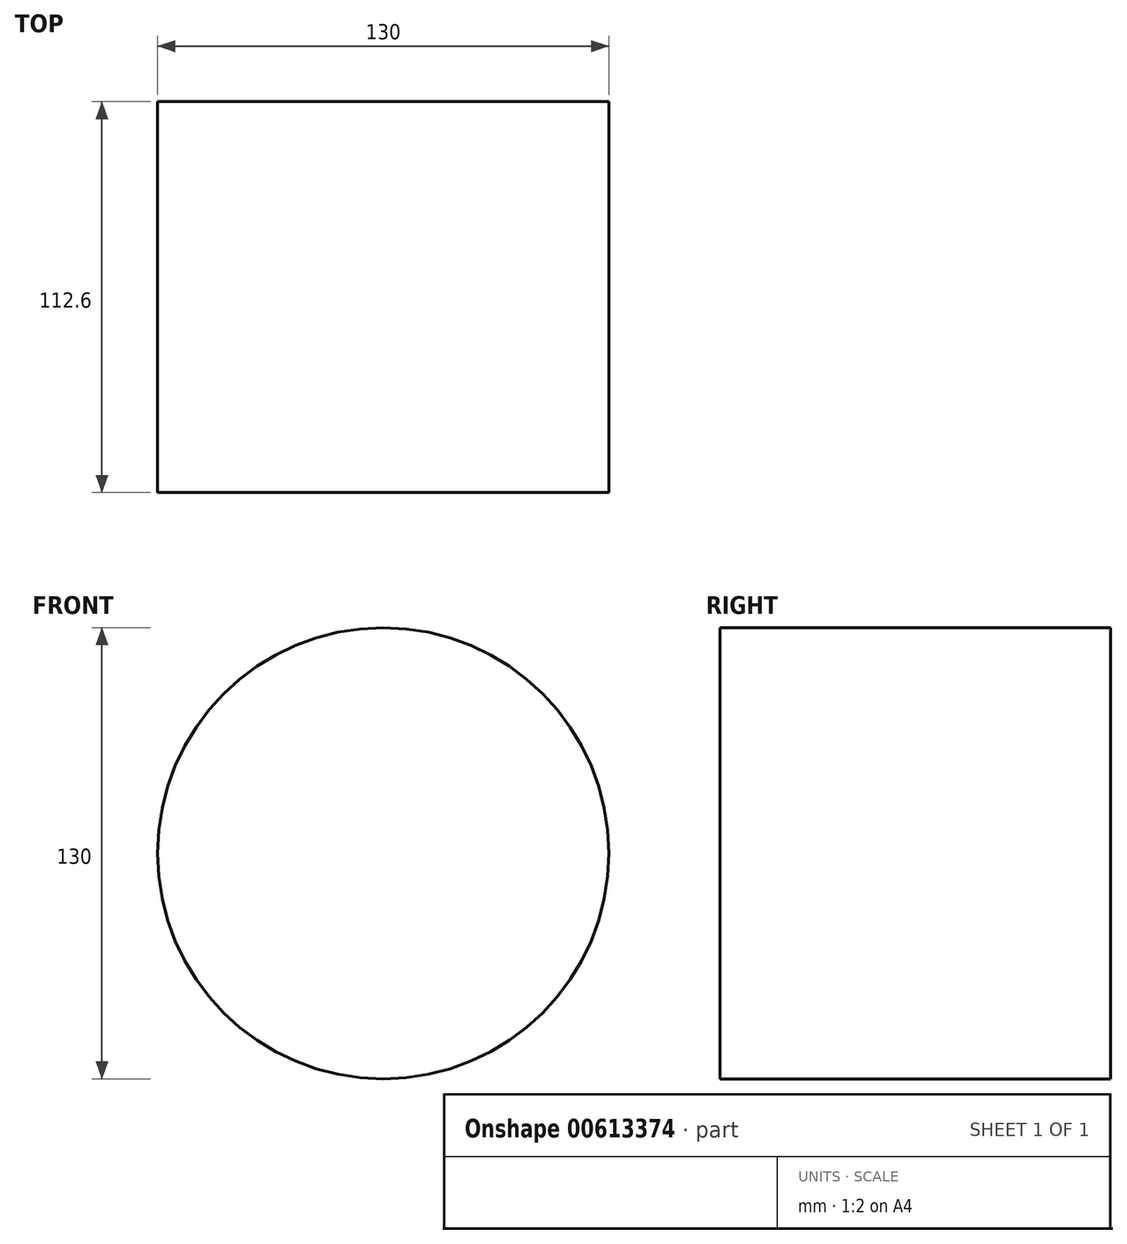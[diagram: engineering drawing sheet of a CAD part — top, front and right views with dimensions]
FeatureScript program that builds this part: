
annotation { "Feature Type Name" : "Feature", "Feature Type Description" : "" }
export const myFeature = defineFeature(function(context is Context, id is Id, definition is map)
    precondition{}
    {
        {
            var Q0;
            Q0=qCreatedBy(makeId("Front.planeOp"),FACE);
            var sketch = newSketch(context, id + "F0", { "sketchPlane" : qUnion([Q0])});
            skCircle(sketch, "E0", {"center": v(0, 0) * mm, "radius": 65 * mm});
            skSolve(sketch);
        }
        {
            var Q0;
            Q0=makeQuery(id+"F0.imprint","IMPRINT",FACE,{"disambiguationData":[TD([[makeQuery(id+"F0.imprint","IMPRINT",EDGE,{"derivedFrom":sQuery(id+"F0.wireOp",EDGE,"E0")}),1.0]])]});
            extrude(context, id + "F1", {"entities" : qUnion([Q0]), "depth" : 112.6 * mm, "offsetDistance" : 25 * mm});
        }
    });
